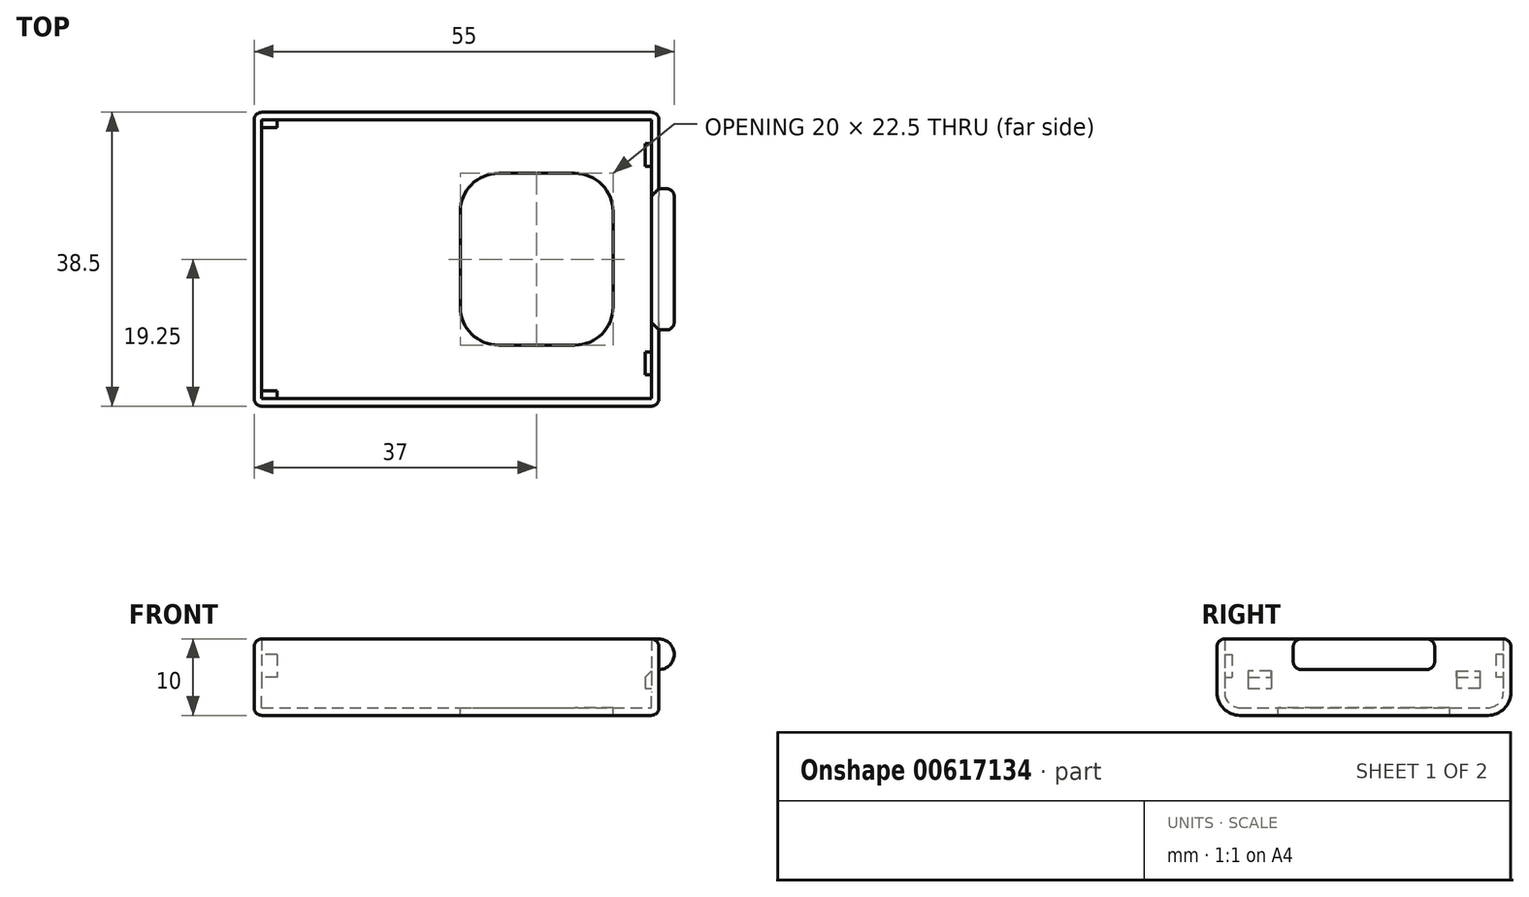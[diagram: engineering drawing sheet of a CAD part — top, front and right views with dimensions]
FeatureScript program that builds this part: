
annotation { "Feature Type Name" : "Feature", "Feature Type Description" : "" }
export const myFeature = defineFeature(function(context is Context, id is Id, definition is map)
    precondition{}
    {
        {
            var Q0;
            Q0=qCreatedBy(makeId("Top.planeOp"),FACE);
            var sketch = newSketch(context, id + "F0", { "sketchPlane" : qUnion([Q0])});
            skLineSegment(sketch, "E0.bottom", {"start": v(0, 0) * mm, "end": v(53, 0) * mm});
            skLineSegment(sketch, "E0.top", {"start": v(0, 38.5) * mm, "end": v(53, 38.5) * mm});
            skLineSegment(sketch, "E0.left", {"start": v(0, 0) * mm, "end": v(0, 38.5) * mm});
            skLineSegment(sketch, "E0.right", {"start": v(53, 0) * mm, "end": v(53, 38.5) * mm});
            skSolve(sketch);
        }
        {
            var Q0;
            Q0=makeQuery(id+"F0.imprint","IMPRINT",FACE,{"disambiguationData":[TD([[makeQuery(id+"F0.imprint","IMPRINT",EDGE,{"derivedFrom":sQuery(id+"F0.wireOp",EDGE,"E0.bottom")}),1.0]])]});
            extrude(context, id + "F1", {"entities" : qUnion([Q0]), "depth" : 10 * mm, "offsetDistance" : 25 * mm});
        }
        {
            var Q0;
            Q0=makeQuery(id+"F1.opExtrude","CAP_EDGE",EDGE,{"disambiguationData":[OSD([sQuery(id+"F0.wireOp",EDGE,"E0.bottom")])],"isStart":true});
            var Q1;
            Q1=makeQuery(id+"F1.opExtrude","CAP_EDGE",EDGE,{"disambiguationData":[OSD([sQuery(id+"F0.wireOp",EDGE,"E0.top")])],"isStart":true});
            fillet(context, id + "F2", {"entities" : qUnion([Q0, Q1]), "radius" : 3 * mm, "tangentPropagation" : true, "allowEdgeOverflow" : false});
        }
        {
            var Q0;
            Q0=makeQuery(id+"F1.opExtrude","CAP_FACE",FACE,{"disambiguationData":[OSD([sQuery(id+"F0.wireOp",EDGE,"E0.bottom"),sQuery(id+"F0.wireOp",EDGE,"E0.top"),sQuery(id+"F0.wireOp",EDGE,"E0.left"),sQuery(id+"F0.wireOp",EDGE,"E0.right")])],"isStart":false});
            shell(context, id + "F3", {"entities" : qUnion([Q0]), "thickness" : 1 * mm});
        }
        {
            var Q0;
            Q0=makeQuery(id+"F3.opShell","OFFSET_FACE",FACE,{"disambiguationData":[OSD([sQuery(id+"F0.wireOp",EDGE,"E0.left")])]});
            var sketch = newSketch(context, id + "F4", { "sketchPlane" : qUnion([Q0])});
            skLineSegment(sketch, "E1.bottom", {"start": v(1, 8) * mm, "end": v(2, 8) * mm});
            skLineSegment(sketch, "E1.top", {"start": v(1, 5) * mm, "end": v(2, 5) * mm});
            skLineSegment(sketch, "E1.left", {"start": v(1, 8) * mm, "end": v(1, 5) * mm});
            skLineSegment(sketch, "E1.right", {"start": v(2, 8) * mm, "end": v(2, 5) * mm});
            skLineSegment(sketch, "E2.bottom", {"start": v(37.5, 8) * mm, "end": v(36.5, 8) * mm});
            skLineSegment(sketch, "E2.top", {"start": v(37.5, 5) * mm, "end": v(36.5, 5) * mm});
            skLineSegment(sketch, "E2.left", {"start": v(37.5, 8) * mm, "end": v(37.5, 5) * mm});
            skLineSegment(sketch, "E2.right", {"start": v(36.5, 8) * mm, "end": v(36.5, 5) * mm});
            skSolve(sketch);
        }
        {
            var Q0;
            Q0=makeQuery(id+"F4.imprint","IMPRINT",FACE,{"disambiguationData":[TD([[makeQuery(id+"F4.imprint","IMPRINT",EDGE,{"derivedFrom":sQuery(id+"F4.wireOp",EDGE,"E2.bottom")}),1.0]])]});
            var Q1;
            Q1=makeQuery(id+"F4.imprint","IMPRINT",FACE,{"disambiguationData":[TD([[makeQuery(id+"F4.imprint","IMPRINT",EDGE,{"derivedFrom":sQuery(id+"F4.wireOp",EDGE,"E1.bottom")}),-1.0]])]});
            extrude(context, id + "F5", {"entities" : qUnion([Q0, Q1]), "operationType" : NewBodyOperationType.ADD, "depth" : 2 * mm, "offsetDistance" : 25 * mm});
        }
        {
            var Q0;
            Q0=makeQuery(id+"F3.opShell","OFFSET_FACE",FACE,{"disambiguationData":[OSD([sQuery(id+"F0.wireOp",EDGE,"E0.right")])]});
            var sketch = newSketch(context, id + "F6", { "sketchPlane" : qUnion([Q0])});
            skLineSegment(sketch, "E3.bottom", {"start": v(-34.4, 6) * mm, "end": v(-31.4, 6) * mm});
            skLineSegment(sketch, "E3.top", {"start": v(-34.4, 3.5) * mm, "end": v(-31.4, 3.5) * mm});
            skLineSegment(sketch, "E3.left", {"start": v(-34.4, 6) * mm, "end": v(-34.4, 3.5) * mm});
            skLineSegment(sketch, "E3.right", {"start": v(-31.4, 6) * mm, "end": v(-31.4, 3.5) * mm});
            skLineSegment(sketch, "E4.bottom", {"start": v(-4.1, 6) * mm, "end": v(-7.1, 6) * mm});
            skLineSegment(sketch, "E4.top", {"start": v(-4.1, 3.5) * mm, "end": v(-7.1, 3.5) * mm});
            skLineSegment(sketch, "E4.left", {"start": v(-4.1, 6) * mm, "end": v(-4.1, 3.5) * mm});
            skLineSegment(sketch, "E4.right", {"start": v(-7.1, 6) * mm, "end": v(-7.1, 3.5) * mm});
            skSolve(sketch);
        }
        {
            var Q0;
            Q0=makeQuery(id+"F6.imprint","IMPRINT",FACE,{"disambiguationData":[TD([[makeQuery(id+"F6.imprint","IMPRINT",EDGE,{"derivedFrom":sQuery(id+"F6.wireOp",EDGE,"E3.bottom")}),-1.0]])]});
            var Q1;
            Q1=makeQuery(id+"F6.imprint","IMPRINT",FACE,{"disambiguationData":[TD([[makeQuery(id+"F6.imprint","IMPRINT",EDGE,{"derivedFrom":sQuery(id+"F6.wireOp",EDGE,"E4.bottom")}),1.0]])]});
            extrude(context, id + "F7", {"entities" : qUnion([Q0, Q1]), "operationType" : NewBodyOperationType.ADD, "depth" : 0.8 * mm, "offsetDistance" : 25 * mm});
        }
        {
            var Q0;
            Q0=makeQuery(id+"F3.opShell","OFFSET_FACE",FACE,{"disambiguationData":[OSD([sQuery(id+"F0.wireOp",EDGE,"E0.bottom"),sQuery(id+"F0.wireOp",EDGE,"E0.top"),sQuery(id+"F0.wireOp",EDGE,"E0.left"),sQuery(id+"F0.wireOp",EDGE,"E0.right")])]});
            var sketch = newSketch(context, id + "F8", { "sketchPlane" : qUnion([Q0])});
            skLineSegment(sketch, "E5.bottom", {"start": v(32, 30.5) * mm, "end": v(42, 30.5) * mm});
            skLineSegment(sketch, "E5.top", {"start": v(32, 8) * mm, "end": v(42, 8) * mm});
            skLineSegment(sketch, "E5.left", {"start": v(27, 25.5) * mm, "end": v(27, 13) * mm});
            skLineSegment(sketch, "E5.right", {"start": v(47, 25.5) * mm, "end": v(47, 13) * mm});
            skPoint(sketch, "E6.visualSharp", {"position": v(47, 30.5) * mm});
            skArc(sketch, "E6.filletArc", {"start": v(47, 25.5) * mm, "mid": v(45.54, 29.04) * mm, "end": v(42, 30.5) * mm});
            skPoint(sketch, "E7.visualSharp", {"position": v(47, 8) * mm});
            skArc(sketch, "E7.filletArc", {"start": v(42, 8) * mm, "mid": v(45.54, 9.46) * mm, "end": v(47, 13) * mm});
            skPoint(sketch, "E8.visualSharp", {"position": v(27, 8) * mm});
            skArc(sketch, "E8.filletArc", {"start": v(27, 13) * mm, "mid": v(28.46, 9.46) * mm, "end": v(32, 8) * mm});
            skPoint(sketch, "E9.visualSharp", {"position": v(27, 30.5) * mm});
            skArc(sketch, "E9.filletArc", {"start": v(32, 30.5) * mm, "mid": v(28.46, 29.04) * mm, "end": v(27, 25.5) * mm});
            skSolve(sketch);
        }
        {
            var Q0;
            Q0=makeQuery(id+"F8.imprint","IMPRINT",FACE,{"disambiguationData":[TD([[makeQuery(id+"F8.imprint","IMPRINT",EDGE,{"derivedFrom":sQuery(id+"F8.wireOp",EDGE,"E5.bottom")}),-1.0]])]});
            extrude(context, id + "F9", {"entities" : qUnion([Q0]), "operationType" : NewBodyOperationType.REMOVE, "endBound" : BoundingType.UP_TO_NEXT, "oppositeDirection" : true, "depth" : 25 * mm, "offsetDistance" : 25 * mm});
        }
        {
            var Q0;
            Q0=makeQuery(id+"F7.opExtrude","CAP_EDGE",EDGE,{"disambiguationData":[OSD([sQuery(id+"F6.wireOp",EDGE,"E3.bottom")])],"isStart":false});
            var Q1;
            Q1=makeQuery(id+"F7.opExtrude","CAP_EDGE",EDGE,{"disambiguationData":[OSD([sQuery(id+"F6.wireOp",EDGE,"E4.bottom")])],"isStart":false});
            chamfer(context, id + "F10", {"entities" : qUnion([Q0, Q1]), "width" : 1 * mm, "tangentPropagation" : true});
        }
        {
            var Q0;
            Q0=makeQuery(id+"F1.opExtrude","SWEPT_FACE",FACE,{"disambiguationData":[OSD([sQuery(id+"F0.wireOp",EDGE,"E0.right")])]});
            var sketch = newSketch(context, id + "F11", { "sketchPlane" : qUnion([Q0])});
            skLineSegment(sketch, "E10.bottom", {"start": v(10, 8) * mm, "end": v(28.5, 8) * mm});
            skLineSegment(sketch, "E10.top", {"start": v(10, 10) * mm, "end": v(28.5, 10) * mm});
            skLineSegment(sketch, "E10.left", {"start": v(10, 8) * mm, "end": v(10, 10) * mm});
            skLineSegment(sketch, "E10.right", {"start": v(28.5, 8) * mm, "end": v(28.5, 10) * mm});
            skLineSegment(sketch, "E11", {"start": v(10, 8) * mm, "end": v(28.5, 8) * mm, "construction": true});
            skSolve(sketch);
        }
        {
            var Q0;
            Q0=makeQuery(id+"F11.imprint","IMPRINT",FACE,{"disambiguationData":[TD([[makeQuery(id+"F11.imprint","IMPRINT",EDGE,{"derivedFrom":sQuery(id+"F11.wireOp",EDGE,"E10.bottom")}),1.0]])]});
            var Q1;
            Q1=sQuery(id+"F11.wireOp",EDGE,"E10.bottom");
            revolve(context, id + "F12", {"entities" : qUnion([Q0]), "axis" : qUnion([Q1]), "revolveType" : RevolveType.ONE_DIRECTION, "angle" : 180 * degree});
        }
        {
            var Q0;
            Q0=makeQuery(id+"F1.opExtrude","SWEPT_BODY",BODY,{"disambiguationData":[OSD([sQuery(id+"F0.wireOp",EDGE,"E0.bottom"),sQuery(id+"F0.wireOp",EDGE,"E0.top"),sQuery(id+"F0.wireOp",EDGE,"E0.left"),sQuery(id+"F0.wireOp",EDGE,"E0.right")])]});
            var Q1;
            Q1=makeQuery(id+"F12.opRevolve","SWEPT_BODY",BODY,{"disambiguationData":[OSD([sQuery(id+"F11.wireOp",EDGE,"E10.bottom"),sQuery(id+"F11.wireOp",EDGE,"E10.top"),sQuery(id+"F11.wireOp",EDGE,"E10.left"),sQuery(id+"F11.wireOp",EDGE,"E10.right")])]});
            booleanBodies(context, id + "F13", {"operationType" : BooleanOperationType.UNION, "tools" : qUnion([Q0, Q1])});
        }
        {
            var Q0;
            Q0=makeQuery(id+"F1.opExtrude","CAP_EDGE",EDGE,{"disambiguationData":[OSD([sQuery(id+"F0.wireOp",EDGE,"E0.bottom")])],"isStart":false});
            var Q1;
            {var subQ0=sQuery(id+"F0.wireOp",EDGE,"E0.right");var subQ1=sQuery(id+"F0.wireOp",EDGE,"E0.bottom");Q1=makeQuery(id+"F13.opBoolean","SPLIT",EDGE,{"disambiguationData":[TD([makeQuery(id+"F1.opExtrude","SWEPT_FACE",FACE,{"disambiguationData":[OSD([subQ1])]})])],"derivedFrom":makeQuery(id+"F1.opExtrude","CAP_EDGE",EDGE,{"disambiguationData":[OSD([subQ0])],"isStart":false})});}
            var Q2;
            {var subQ0=sQuery(id+"F0.wireOp",EDGE,"E0.right");var subQ1=sQuery(id+"F0.wireOp",EDGE,"E0.top");Q2=makeQuery(id+"F13.opBoolean","SPLIT",EDGE,{"disambiguationData":[TD([makeQuery(id+"F1.opExtrude","SWEPT_FACE",FACE,{"disambiguationData":[OSD([subQ1])]})])],"derivedFrom":makeQuery(id+"F1.opExtrude","CAP_EDGE",EDGE,{"disambiguationData":[OSD([subQ0])],"isStart":false})});}
            var Q3;
            Q3=makeQuery(id+"F1.opExtrude","CAP_EDGE",EDGE,{"disambiguationData":[OSD([sQuery(id+"F0.wireOp",EDGE,"E0.top")])],"isStart":false});
            var Q4;
            Q4=makeQuery(id+"F1.opExtrude","SWEPT_EDGE",EDGE,{"disambiguationData":[OSD([sQuery(id+"F0.wireOp",EDGE,"E0.top"),sQuery(id+"F0.wireOp",EDGE,"E0.right")])]});
            var Q5;
            Q5=makeQuery(id+"F1.opExtrude","SWEPT_EDGE",EDGE,{"disambiguationData":[OSD([sQuery(id+"F0.wireOp",EDGE,"E0.top"),sQuery(id+"F0.wireOp",EDGE,"E0.left")])]});
            var Q6;
            Q6=makeQuery(id+"F1.opExtrude","CAP_EDGE",EDGE,{"disambiguationData":[OSD([sQuery(id+"F0.wireOp",EDGE,"E0.left")])],"isStart":false});
            var Q7;
            Q7=makeQuery(id+"F9.boolean.opBoolean","COPY",EDGE,{"derivedFrom":makeQuery(id+"F9.opExtrude","CAP_EDGE",EDGE,{"disambiguationData":[OSD([sQuery(id+"F8.wireOp",EDGE,"E5.right")])],"isStart":false})});
            var Q8;
            Q8=makeQuery(id+"F12.opRevolve","SWEPT_EDGE",EDGE,{"disambiguationData":[OSD([sQuery(id+"F0.wireOp",EDGE,"E0.right"),sQuery(id+"F11.wireOp",EDGE,"E10.top"),sQuery(id+"F11.wireOp",EDGE,"E10.left")])]});
            var Q9;
            Q9=makeQuery(id+"F12.opRevolve","SWEPT_EDGE",EDGE,{"disambiguationData":[OSD([sQuery(id+"F0.wireOp",EDGE,"E0.right"),sQuery(id+"F11.wireOp",EDGE,"E10.top"),sQuery(id+"F11.wireOp",EDGE,"E10.right")])]});
            fillet(context, id + "F14", {"entities" : qUnion([Q0, Q1, Q2, Q3, Q4, Q5, Q6, Q7, Q8, Q9]), "radius" : 1 * mm, "tangentPropagation" : true, "allowEdgeOverflow" : false});
        }
    });
